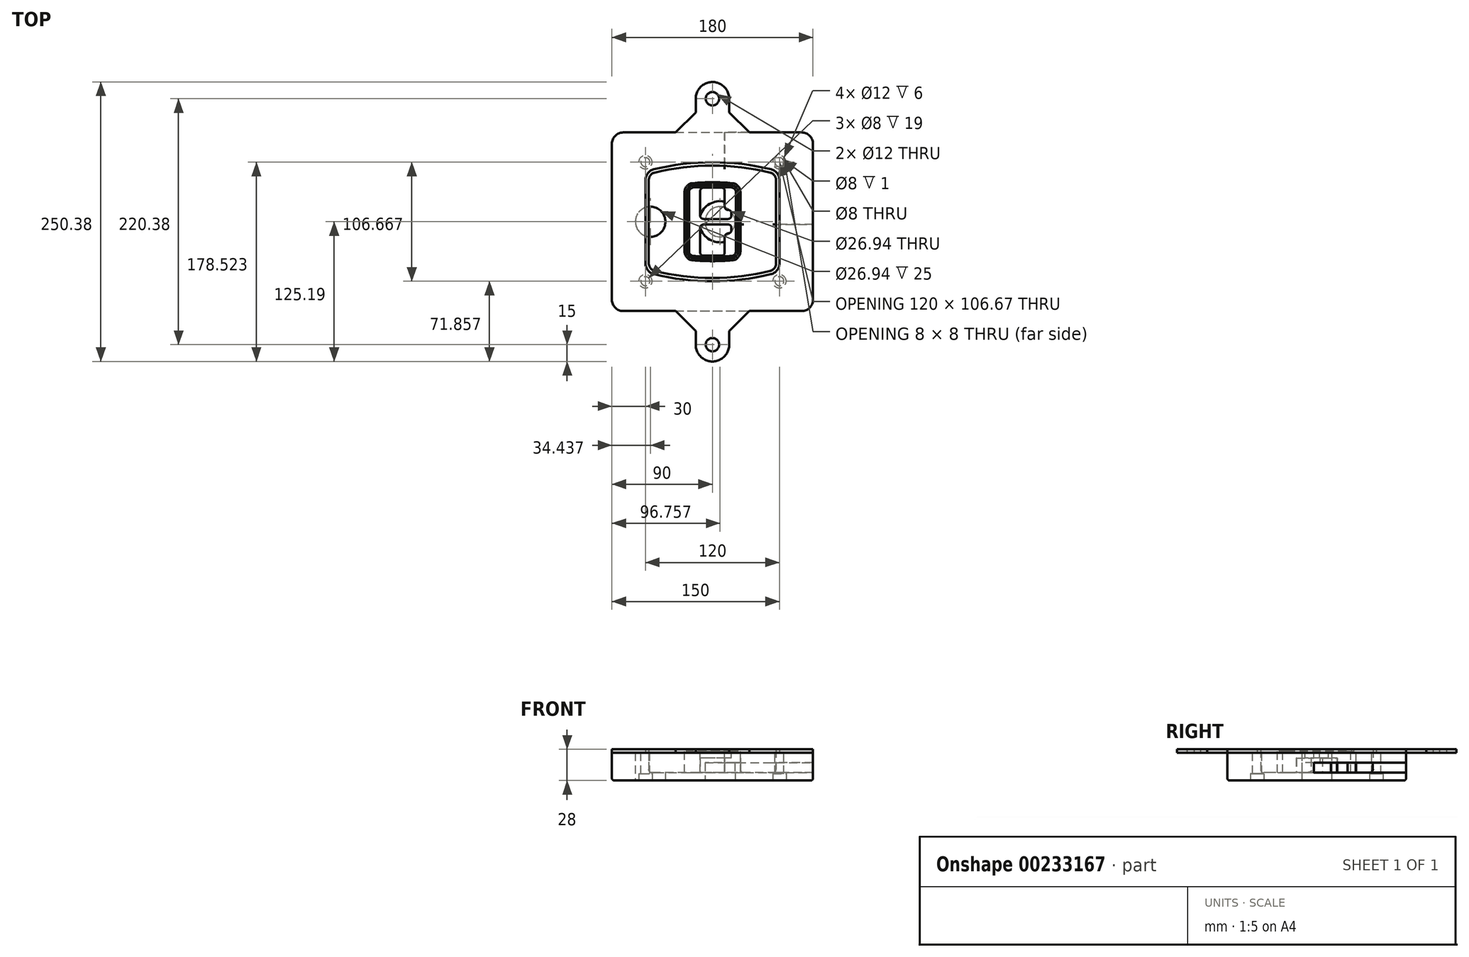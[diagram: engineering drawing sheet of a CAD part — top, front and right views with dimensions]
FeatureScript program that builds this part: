
annotation { "Feature Type Name" : "Feature", "Feature Type Description" : "" }
export const myFeature = defineFeature(function(context is Context, id is Id, definition is map)
    precondition{}
    {
        {
            var Q0;
            Q0=qCreatedBy(makeId("Top.planeOp"),FACE);
            var sketch = newSketch(context, id + "F0", { "sketchPlane" : qUnion([Q0])});
            skPoint(sketch, "E0.rect.middle", {"position": v(0, 0) * mm});
            skLineSegment(sketch, "E1.bottom", {"start": v(-80, -80) * mm, "end": v(80, -80) * mm});
            skLineSegment(sketch, "E1.top", {"start": v(-80, 80) * mm, "end": v(80, 80) * mm});
            skLineSegment(sketch, "E1.left", {"start": v(-90, -70) * mm, "end": v(-90, 70) * mm});
            skLineSegment(sketch, "E1.right", {"start": v(90, -70) * mm, "end": v(90, 70) * mm});
            skLineSegment(sketch, "E2", {"start": v(-90, 80) * mm, "end": v(90, -80) * mm, "construction": true});
            skLineSegment(sketch, "E3", {"start": v(90, 80) * mm, "end": v(-90, -80) * mm, "construction": true});
            skCircle(sketch, "E4", {"center": v(-60, 53.33) * mm, "radius": 4 * mm});
            skCircle(sketch, "E5", {"center": v(60, 53.33) * mm, "radius": 4 * mm});
            skCircle(sketch, "E6", {"center": v(60, -53.33) * mm, "radius": 4 * mm});
            skCircle(sketch, "E7", {"center": v(-60, -53.33) * mm, "radius": 4 * mm});
            skLineSegment(sketch, "E8", {"start": v(-60, 53.33) * mm, "end": v(60, 53.33) * mm, "construction": true});
            skLineSegment(sketch, "E9", {"start": v(60, 53.33) * mm, "end": v(60, -53.33) * mm, "construction": true});
            skLineSegment(sketch, "E10", {"start": v(60, -53.33) * mm, "end": v(-60, -53.33) * mm, "construction": true});
            skLineSegment(sketch, "E11", {"start": v(-60, -53.33) * mm, "end": v(-60, 53.33) * mm, "construction": true});
            skLineSegment(sketch, "E12", {"start": v(-60, 37.3) * mm, "end": v(-60, -37.3) * mm});
            skLineSegment(sketch, "E13", {"start": v(60, 37.3) * mm, "end": v(60, -37.3) * mm});
            skArc(sketch, "E14", {"start": v(52.38, 47.01) * mm, "mid": v(0, 53.33) * mm, "end": v(-52.38, 47.01) * mm});
            skArc(sketch, "E15", {"start": v(-52.38, -47.01) * mm, "mid": v(0, -53.33) * mm, "end": v(52.38, -47.01) * mm});
            skLineSegment(sketch, "E16", {"start": v(-60, 0) * mm, "end": v(60, 0) * mm, "construction": true});
            skPoint(sketch, "E17.visualSharp", {"position": v(-60, -45) * mm});
            skArc(sketch, "E17.filletArc", {"start": v(-60, -37.3) * mm, "mid": v(-57.87, -43.47) * mm, "end": v(-52.38, -47.01) * mm});
            skPoint(sketch, "E18.visualSharp", {"position": v(-60, 45) * mm});
            skArc(sketch, "E18.filletArc", {"start": v(-52.38, 47.01) * mm, "mid": v(-57.87, 43.47) * mm, "end": v(-60, 37.3) * mm});
            skPoint(sketch, "E19.visualSharp", {"position": v(60, 45) * mm});
            skArc(sketch, "E19.filletArc", {"start": v(60, 37.3) * mm, "mid": v(57.87, 43.47) * mm, "end": v(52.38, 47.01) * mm});
            skPoint(sketch, "E20.visualSharp", {"position": v(60, -45) * mm});
            skArc(sketch, "E20.filletArc", {"start": v(52.38, -47.01) * mm, "mid": v(57.87, -43.47) * mm, "end": v(60, -37.3) * mm});
            skPoint(sketch, "E21.visualSharp", {"position": v(-90, 80) * mm});
            skArc(sketch, "E21.filletArc", {"start": v(-80, 80) * mm, "mid": v(-87.07, 77.07) * mm, "end": v(-90, 70) * mm});
            skPoint(sketch, "E22.visualSharp", {"position": v(90, 80) * mm});
            skArc(sketch, "E22.filletArc", {"start": v(90, 70) * mm, "mid": v(87.07, 77.07) * mm, "end": v(80, 80) * mm});
            skPoint(sketch, "E23.visualSharp", {"position": v(90, -80) * mm});
            skArc(sketch, "E23.filletArc", {"start": v(80, -80) * mm, "mid": v(87.07, -77.07) * mm, "end": v(90, -70) * mm});
            skPoint(sketch, "E24.visualSharp", {"position": v(-90, -80) * mm});
            skArc(sketch, "E24.filletArc", {"start": v(-90, -70) * mm, "mid": v(-87.07, -77.07) * mm, "end": v(-80, -80) * mm});
            skArc(sketch, "E25.0", {"start": v(57, 37.3) * mm, "mid": v(55.5, 41.62) * mm, "end": v(51.67, 44.1) * mm});
            skLineSegment(sketch, "E25.1", {"start": v(57, 37.3) * mm, "end": v(57, -37.3) * mm});
            skArc(sketch, "E25.2", {"start": v(51.67, -44.1) * mm, "mid": v(55.5, -41.62) * mm, "end": v(57, -37.3) * mm});
            skArc(sketch, "E25.3", {"start": v(-51.67, -44.1) * mm, "mid": v(0, -50.33) * mm, "end": v(51.67, -44.1) * mm});
            skArc(sketch, "E25.4", {"start": v(-57, -37.3) * mm, "mid": v(-55.5, -41.62) * mm, "end": v(-51.67, -44.1) * mm});
            skArc(sketch, "E25.5", {"start": v(51.67, 44.1) * mm, "mid": v(0, 50.33) * mm, "end": v(-51.67, 44.1) * mm});
            skLineSegment(sketch, "E25.6", {"start": v(-57, 37.3) * mm, "end": v(-57, -37.3) * mm});
            skArc(sketch, "E25.7", {"start": v(-51.67, 44.1) * mm, "mid": v(-55.5, 41.62) * mm, "end": v(-57, 37.3) * mm});
            skArc(sketch, "E26.0", {"start": v(-53.33, 50.9) * mm, "mid": v(-61.01, 45.94) * mm, "end": v(-64, 37.3) * mm});
            skArc(sketch, "E26.1", {"start": v(53.33, 50.9) * mm, "mid": v(0, 57.33) * mm, "end": v(-53.33, 50.9) * mm});
            skArc(sketch, "E26.2", {"start": v(64, 37.3) * mm, "mid": v(61.01, 45.94) * mm, "end": v(53.33, 50.9) * mm});
            skLineSegment(sketch, "E26.3", {"start": v(64, 37.3) * mm, "end": v(64, -37.3) * mm});
            skArc(sketch, "E26.4", {"start": v(53.33, -50.9) * mm, "mid": v(61.01, -45.94) * mm, "end": v(64, -37.3) * mm});
            skLineSegment(sketch, "E26.5", {"start": v(-64, 37.3) * mm, "end": v(-64, -37.3) * mm});
            skArc(sketch, "E26.6", {"start": v(-53.33, -50.9) * mm, "mid": v(0, -57.33) * mm, "end": v(53.33, -50.9) * mm});
            skArc(sketch, "E26.7", {"start": v(-64, -37.3) * mm, "mid": v(-61.01, -45.94) * mm, "end": v(-53.33, -50.9) * mm});
            skSolve(sketch);
        }
        {
            var Q0;
            Q0=makeQuery(id+"F0.imprint","IMPRINT",FACE,{"disambiguationData":[TD([[makeQuery(id+"F0.imprint","IMPRINT",EDGE,{"derivedFrom":sQuery(id+"F0.wireOp",EDGE,"E1.bottom")}),1.0]])]});
            var Q1;
            Q1=makeQuery(id+"F0.imprint","IMPRINT",FACE,{"disambiguationData":[TD([[makeQuery(id+"F0.imprint","IMPRINT",EDGE,{"derivedFrom":sQuery(id+"F0.wireOp",EDGE,"E12")}),1.0]])]});
            var Q2;
            Q2=makeQuery(id+"F0.imprint","IMPRINT",FACE,{"disambiguationData":[TD([[makeQuery(id+"F0.imprint","IMPRINT",EDGE,{"derivedFrom":sQuery(id+"F0.wireOp",EDGE,"E25.0")}),1.0]])]});
            var Q3;
            Q3=makeQuery(id+"F0.imprint","IMPRINT",FACE,{"disambiguationData":[TD([[makeQuery(id+"F0.imprint","IMPRINT",EDGE,{"derivedFrom":sQuery(id+"F0.wireOp",EDGE,"E12")}),-1.0]])]});
            extrude(context, id + "F1", {"entities" : qUnion([Q0, Q1, Q2, Q3]), "oppositeDirection" : true, "depth" : 25 * mm});
        }
        {
            var Q0;
            Q0=makeQuery(id+"F0.imprint","IMPRINT",FACE,{"disambiguationData":[TD([[makeQuery(id+"F0.imprint","IMPRINT",EDGE,{"derivedFrom":sQuery(id+"F0.wireOp",EDGE,"E12")}),1.0]])]});
            extrude(context, id + "F2", {"entities" : qUnion([Q0]), "operationType" : NewBodyOperationType.ADD, "depth" : 3 * mm});
        }
        {
            var Q0;
            Q0=makeQuery(id+"F0.imprint","IMPRINT",FACE,{"disambiguationData":[TD([[makeQuery(id+"F0.imprint","IMPRINT",EDGE,{"derivedFrom":sQuery(id+"F0.wireOp",EDGE,"E25.0")}),1.0]])]});
            extrude(context, id + "F3", {"entities" : qUnion([Q0]), "operationType" : NewBodyOperationType.REMOVE, "oppositeDirection" : true, "depth" : 18 * mm});
        }
        {
            var Q0;
            Q0=makeQuery(id+"F2.opExtrude","CAP_FACE",FACE,{"disambiguationData":[OSD([sQuery(id+"F0.wireOp",EDGE,"E12"),sQuery(id+"F0.wireOp",EDGE,"E13"),sQuery(id+"F0.wireOp",EDGE,"E14"),sQuery(id+"F0.wireOp",EDGE,"E15"),sQuery(id+"F0.wireOp",EDGE,"E17.filletArc"),sQuery(id+"F0.wireOp",EDGE,"E18.filletArc"),sQuery(id+"F0.wireOp",EDGE,"E19.filletArc"),sQuery(id+"F0.wireOp",EDGE,"E20.filletArc"),sQuery(id+"F0.wireOp",EDGE,"E25.0"),sQuery(id+"F0.wireOp",EDGE,"E25.1"),sQuery(id+"F0.wireOp",EDGE,"E25.2"),sQuery(id+"F0.wireOp",EDGE,"E25.3"),sQuery(id+"F0.wireOp",EDGE,"E25.4"),sQuery(id+"F0.wireOp",EDGE,"E25.5"),sQuery(id+"F0.wireOp",EDGE,"E25.6"),sQuery(id+"F0.wireOp",EDGE,"E25.7")])],"isStart":false});
            var sketch = newSketch(context, id + "F4", { "sketchPlane" : qUnion([Q0])});
            skArc(sketch, "E27.0", {"start": v(-17.7, -34.56) * mm, "mid": v(0, -35.33) * mm, "end": v(17.7, -34.56) * mm});
            skArc(sketch, "E28.0", {"start": v(17.7, 34.56) * mm, "mid": v(0, 35.33) * mm, "end": v(-17.7, 34.56) * mm});
            skLineSegment(sketch, "E29", {"start": v(-25, 26.59) * mm, "end": v(-25, -26.59) * mm});
            skLineSegment(sketch, "E30", {"start": v(25, 26.59) * mm, "end": v(25, -26.59) * mm});
            skLineSegment(sketch, "E31", {"start": v(-25, 33.78) * mm, "end": v(25, 33.78) * mm, "construction": true});
            skLineSegment(sketch, "E32", {"start": v(-25, -33.78) * mm, "end": v(25, -33.78) * mm, "construction": true});
            skPoint(sketch, "E33.visualSharp", {"position": v(-25, 33.78) * mm});
            skArc(sketch, "E33.filletArc", {"start": v(-17.7, 34.56) * mm, "mid": v(-22.9, 32) * mm, "end": v(-25, 26.59) * mm});
            skPoint(sketch, "E34.visualSharp", {"position": v(25, 33.78) * mm});
            skArc(sketch, "E34.filletArc", {"start": v(25, 26.59) * mm, "mid": v(22.9, 32) * mm, "end": v(17.7, 34.56) * mm});
            skPoint(sketch, "E35.visualSharp", {"position": v(25, -33.78) * mm});
            skArc(sketch, "E35.filletArc", {"start": v(17.7, -34.56) * mm, "mid": v(22.9, -32) * mm, "end": v(25, -26.59) * mm});
            skPoint(sketch, "E36.visualSharp", {"position": v(-25, -33.78) * mm});
            skArc(sketch, "E36.filletArc", {"start": v(-25, -26.59) * mm, "mid": v(-22.9, -32) * mm, "end": v(-17.7, -34.56) * mm});
            skArc(sketch, "E37.0", {"start": v(51.67, 44.1) * mm, "mid": v(0, 50.33) * mm, "end": v(-51.67, 44.1) * mm});
            skArc(sketch, "E37.1", {"start": v(-51.67, 44.1) * mm, "mid": v(-55.5, 41.62) * mm, "end": v(-57, 37.3) * mm});
            skLineSegment(sketch, "E37.2", {"start": v(-57, 37.3) * mm, "end": v(-57, -37.3) * mm});
            skArc(sketch, "E37.3", {"start": v(-57, -37.3) * mm, "mid": v(-55.5, -41.62) * mm, "end": v(-51.67, -44.1) * mm});
            skArc(sketch, "E37.4", {"start": v(-51.67, -44.1) * mm, "mid": v(0, -50.33) * mm, "end": v(51.67, -44.1) * mm});
            skArc(sketch, "E37.5", {"start": v(51.67, -44.1) * mm, "mid": v(55.5, -41.62) * mm, "end": v(57, -37.3) * mm});
            skLineSegment(sketch, "E37.6", {"start": v(57, 37.3) * mm, "end": v(57, -37.3) * mm});
            skArc(sketch, "E37.7", {"start": v(57, 37.3) * mm, "mid": v(55.5, 41.62) * mm, "end": v(51.67, 44.1) * mm});
            skLineSegment(sketch, "E38.0", {"start": v(23, 26.59) * mm, "end": v(23, -26.59) * mm});
            skArc(sketch, "E38.1", {"start": v(17.53, -32.56) * mm, "mid": v(21.42, -30.64) * mm, "end": v(23, -26.59) * mm});
            skArc(sketch, "E38.2", {"start": v(-17.53, -32.56) * mm, "mid": v(0, -33.33) * mm, "end": v(17.53, -32.56) * mm});
            skArc(sketch, "E38.3", {"start": v(-23, -26.59) * mm, "mid": v(-21.42, -30.64) * mm, "end": v(-17.53, -32.56) * mm});
            skLineSegment(sketch, "E38.4", {"start": v(-23, 26.59) * mm, "end": v(-23, -26.59) * mm});
            skArc(sketch, "E38.5", {"start": v(23, 26.59) * mm, "mid": v(21.42, 30.64) * mm, "end": v(17.53, 32.56) * mm});
            skArc(sketch, "E38.6", {"start": v(-17.53, 32.56) * mm, "mid": v(-21.42, 30.64) * mm, "end": v(-23, 26.59) * mm});
            skArc(sketch, "E38.7", {"start": v(17.53, 32.56) * mm, "mid": v(0, 33.33) * mm, "end": v(-17.53, 32.56) * mm});
            skArc(sketch, "E39.0", {"start": v(21, 26.59) * mm, "mid": v(19.95, 29.29) * mm, "end": v(17.35, 30.57) * mm});
            skLineSegment(sketch, "E39.1", {"start": v(21, 26.59) * mm, "end": v(21, -26.59) * mm});
            skArc(sketch, "E39.2", {"start": v(17.35, -30.57) * mm, "mid": v(19.95, -29.29) * mm, "end": v(21, -26.59) * mm});
            skArc(sketch, "E39.3", {"start": v(-17.35, -30.57) * mm, "mid": v(0, -31.33) * mm, "end": v(17.35, -30.57) * mm});
            skArc(sketch, "E39.4", {"start": v(-21, -26.59) * mm, "mid": v(-19.95, -29.29) * mm, "end": v(-17.35, -30.57) * mm});
            skArc(sketch, "E39.5", {"start": v(17.35, 30.57) * mm, "mid": v(0, 31.33) * mm, "end": v(-17.35, 30.57) * mm});
            skLineSegment(sketch, "E39.6", {"start": v(-21, 26.59) * mm, "end": v(-21, -26.59) * mm});
            skArc(sketch, "E39.7", {"start": v(-17.35, 30.57) * mm, "mid": v(-19.95, 29.29) * mm, "end": v(-21, 26.59) * mm});
            skLineSegment(sketch, "E40", {"start": v(-25, 0) * mm, "end": v(25, 0) * mm, "construction": true});
            skLineSegment(sketch, "E41", {"start": v(-11, 5.5) * mm, "end": v(-11, 27.5) * mm});
            skLineSegment(sketch, "E42", {"start": v(-8, 30.5) * mm, "end": v(8, 30.5) * mm});
            skLineSegment(sketch, "E43", {"start": v(11, 27.5) * mm, "end": v(11, 13.5) * mm});
            skLineSegment(sketch, "E44", {"start": v(14, 10.5) * mm, "end": v(14, 10.5) * mm});
            skLineSegment(sketch, "E45", {"start": v(17, 7.5) * mm, "end": v(17, 5.5) * mm});
            skLineSegment(sketch, "E46", {"start": v(14, 2.5) * mm, "end": v(-8, 2.5) * mm});
            skPoint(sketch, "E47.visualSharp", {"position": v(-11, 30.5) * mm});
            skArc(sketch, "E47.filletArc", {"start": v(-8, 30.5) * mm, "mid": v(-10.12, 29.62) * mm, "end": v(-11, 27.5) * mm});
            skPoint(sketch, "E48.visualSharp", {"position": v(11, 30.5) * mm});
            skArc(sketch, "E48.filletArc", {"start": v(11, 27.5) * mm, "mid": v(10.12, 29.62) * mm, "end": v(8, 30.5) * mm});
            skPoint(sketch, "E49.visualSharp", {"position": v(11, 10.5) * mm});
            skArc(sketch, "E49.filletArc", {"start": v(11, 13.5) * mm, "mid": v(11.88, 11.38) * mm, "end": v(14, 10.5) * mm});
            skPoint(sketch, "E50.visualSharp", {"position": v(17, 10.5) * mm});
            skArc(sketch, "E50.filletArc", {"start": v(17, 7.5) * mm, "mid": v(16.12, 9.62) * mm, "end": v(14, 10.5) * mm});
            skPoint(sketch, "E51.visualSharp", {"position": v(17, 2.5) * mm});
            skArc(sketch, "E51.filletArc", {"start": v(14, 2.5) * mm, "mid": v(16.12, 3.38) * mm, "end": v(17, 5.5) * mm});
            skPoint(sketch, "E52.visualSharp", {"position": v(-11, 2.5) * mm});
            skArc(sketch, "E52.filletArc", {"start": v(-11, 5.5) * mm, "mid": v(-10.12, 3.38) * mm, "end": v(-8, 2.5) * mm});
            skLineSegment(sketch, "E53.0.MirrorCS", {"start": v(14, -2.5) * mm, "end": v(-8, -2.5) * mm});
            skArc(sketch, "E54.0.MirrorCS", {"start": v(-11, -5.5) * mm, "mid": v(-10.12, -3.38) * mm, "end": v(-8, -2.5) * mm});
            skLineSegment(sketch, "E55.0.MirrorCS", {"start": v(-11, -5.5) * mm, "end": v(-11, -27.5) * mm});
            skArc(sketch, "E56.0.MirrorCS", {"start": v(-8, -30.5) * mm, "mid": v(-10.12, -29.62) * mm, "end": v(-11, -27.5) * mm});
            skLineSegment(sketch, "E57.0.MirrorCS", {"start": v(-8, -30.5) * mm, "end": v(8, -30.5) * mm});
            skArc(sketch, "E58.0.MirrorCS", {"start": v(11, -27.5) * mm, "mid": v(10.12, -29.62) * mm, "end": v(8, -30.5) * mm});
            skLineSegment(sketch, "E59.0.MirrorCS", {"start": v(11, -27.5) * mm, "end": v(11, -13.5) * mm});
            skArc(sketch, "E60.0.MirrorCS", {"start": v(11, -13.5) * mm, "mid": v(11.88, -11.38) * mm, "end": v(14, -10.5) * mm});
            skArc(sketch, "E61.0.MirrorCS", {"start": v(17, -7.5) * mm, "mid": v(16.12, -9.62) * mm, "end": v(14, -10.5) * mm});
            skLineSegment(sketch, "E62.0.MirrorCS", {"start": v(17, -7.5) * mm, "end": v(17, -5.5) * mm});
            skArc(sketch, "E63.0.MirrorCS", {"start": v(14, -2.5) * mm, "mid": v(16.12, -3.38) * mm, "end": v(17, -5.5) * mm});
            skSolve(sketch);
        }
        {
            var Q0;
            Q0=makeQuery(id+"F4.imprint","IMPRINT",FACE,{"disambiguationData":[TD([[makeQuery(id+"F4.imprint","IMPRINT",EDGE,{"derivedFrom":sQuery(id+"F4.wireOp",EDGE,"E27.0")}),1.0]])]});
            var Q1;
            Q1=makeQuery(id+"F4.imprint","IMPRINT",FACE,{"disambiguationData":[TD([[makeQuery(id+"F4.imprint","IMPRINT",EDGE,{"derivedFrom":sQuery(id+"F4.wireOp",EDGE,"E38.0")}),-1.0]])]});
            var Q2;
            Q2=makeQuery(id+"F4.imprint","IMPRINT",FACE,{"disambiguationData":[TD([[makeQuery(id+"F4.imprint","IMPRINT",EDGE,{"derivedFrom":sQuery(id+"F4.wireOp",EDGE,"E39.0")}),1.0]])]});
            extrude(context, id + "F5", {"entities" : qUnion([Q0, Q1, Q2]), "operationType" : NewBodyOperationType.ADD, "endBound" : BoundingType.UP_TO_NEXT, "oppositeDirection" : true, "depth" : 25 * mm});
        }
        {
            var Q0;
            Q0=makeQuery(id+"F4.imprint","IMPRINT",FACE,{"disambiguationData":[TD([[makeQuery(id+"F4.imprint","IMPRINT",EDGE,{"derivedFrom":sQuery(id+"F4.wireOp",EDGE,"E38.0")}),-1.0]])]});
            extrude(context, id + "F6", {"entities" : qUnion([Q0]), "operationType" : NewBodyOperationType.REMOVE, "oppositeDirection" : true, "depth" : 2 * mm});
        }
        {
            var Q0;
            Q0=makeQuery(id+"F1.opExtrude","CAP_FACE",FACE,{"disambiguationData":[OSD([sQuery(id+"F0.wireOp",EDGE,"E1.bottom"),sQuery(id+"F0.wireOp",EDGE,"E1.top"),sQuery(id+"F0.wireOp",EDGE,"E1.left"),sQuery(id+"F0.wireOp",EDGE,"E1.right"),sQuery(id+"F0.wireOp",EDGE,"E4"),sQuery(id+"F0.wireOp",EDGE,"E5"),sQuery(id+"F0.wireOp",EDGE,"E6"),sQuery(id+"F0.wireOp",EDGE,"E7"),sQuery(id+"F0.wireOp",EDGE,"E21.filletArc"),sQuery(id+"F0.wireOp",EDGE,"E22.filletArc"),sQuery(id+"F0.wireOp",EDGE,"E23.filletArc"),sQuery(id+"F0.wireOp",EDGE,"E24.filletArc")])],"isStart":false});
            var sketch = newSketch(context, id + "F7", { "sketchPlane" : qUnion([Q0])});
            skCircle(sketch, "E64", {"center": v(6.76, 0) * mm, "radius": 13.47 * mm});
            skCircle(sketch, "E65", {"center": v(-55.56, 0) * mm, "radius": 13.47 * mm});
            skLineSegment(sketch, "E66", {"start": v(90, 0) * mm, "end": v(-90, 0) * mm});
            skCircle(sketch, "E67", {"center": v(6.76, 0) * mm, "radius": 18.47 * mm});
            skCircle(sketch, "E68", {"center": v(60, -53.33) * mm, "radius": 6 * mm});
            skCircle(sketch, "E69", {"center": v(-60, -53.33) * mm, "radius": 6 * mm});
            skCircle(sketch, "E70", {"center": v(-60, 53.33) * mm, "radius": 6 * mm});
            skCircle(sketch, "E71", {"center": v(60, 53.33) * mm, "radius": 6 * mm});
            skSolve(sketch);
        }
        {
            var Q0;
            {var subQ1=sQuery(id+"F7.wireOp",EDGE,"E66");var subQ4=sQuery(id+"F7.wireOp",EDGE,"E64");var subQ6=makeQuery(id+"F7.imprint","INTERSECT",VERTEX,{"disambiguationData":[OD(0.0)],"derivedFrom":[subQ4,subQ1]});Q0=makeQuery(id+"F7.imprint","IMPRINT",FACE,{"disambiguationData":[TD([[makeQuery(id+"F7.imprint","IMPRINT",EDGE,{"disambiguationData":[TD([[subQ6,-1.0]])],"derivedFrom":subQ4}),-1.0]])]});}
            var Q1;
            {var subQ0=sQuery(id+"F7.wireOp",EDGE,"E66");var subQ1=sQuery(id+"F7.wireOp",EDGE,"E64");var subQ3=makeQuery(id+"F7.imprint","INTERSECT",VERTEX,{"disambiguationData":[OD(0.0)],"derivedFrom":[subQ1,subQ0]});Q1=makeQuery(id+"F7.imprint","IMPRINT",FACE,{"disambiguationData":[TD([[makeQuery(id+"F7.imprint","IMPRINT",EDGE,{"disambiguationData":[TD([[subQ3,-1.0]])],"derivedFrom":subQ1}),1.0]])]});}
            var Q2;
            {var subQ0=sQuery(id+"F7.wireOp",EDGE,"E66");var subQ1=sQuery(id+"F7.wireOp",EDGE,"E64");var subQ3=makeQuery(id+"F7.imprint","INTERSECT",VERTEX,{"disambiguationData":[OD(0.0)],"derivedFrom":[subQ1,subQ0]});Q2=makeQuery(id+"F7.imprint","IMPRINT",FACE,{"disambiguationData":[TD([[makeQuery(id+"F7.imprint","IMPRINT",EDGE,{"disambiguationData":[TD([[subQ3,1.0]])],"derivedFrom":subQ1}),1.0]])]});}
            var Q3;
            {var subQ1=sQuery(id+"F7.wireOp",EDGE,"E66");var subQ4=sQuery(id+"F7.wireOp",EDGE,"E64");var subQ6=makeQuery(id+"F7.imprint","INTERSECT",VERTEX,{"disambiguationData":[OD(0.0)],"derivedFrom":[subQ4,subQ1]});Q3=makeQuery(id+"F7.imprint","IMPRINT",FACE,{"disambiguationData":[TD([[makeQuery(id+"F7.imprint","IMPRINT",EDGE,{"disambiguationData":[TD([[subQ6,1.0]])],"derivedFrom":subQ4}),-1.0]])]});}
            extrude(context, id + "F8", {"entities" : qUnion([Q0, Q1, Q2, Q3]), "operationType" : NewBodyOperationType.ADD, "oppositeDirection" : true, "depth" : 20 * mm});
        }
        {
            var Q0;
            {var subQ0=sQuery(id+"F7.wireOp",EDGE,"E66");var subQ1=sQuery(id+"F7.wireOp",EDGE,"E64");var subQ3=makeQuery(id+"F7.imprint","INTERSECT",VERTEX,{"disambiguationData":[OD(0.0)],"derivedFrom":[subQ1,subQ0]});Q0=makeQuery(id+"F7.imprint","IMPRINT",FACE,{"disambiguationData":[TD([[makeQuery(id+"F7.imprint","IMPRINT",EDGE,{"disambiguationData":[TD([[subQ3,-1.0]])],"derivedFrom":subQ1}),1.0]])]});}
            var Q1;
            {var subQ0=sQuery(id+"F7.wireOp",EDGE,"E66");var subQ1=sQuery(id+"F7.wireOp",EDGE,"E64");var subQ3=makeQuery(id+"F7.imprint","INTERSECT",VERTEX,{"disambiguationData":[OD(0.0)],"derivedFrom":[subQ1,subQ0]});Q1=makeQuery(id+"F7.imprint","IMPRINT",FACE,{"disambiguationData":[TD([[makeQuery(id+"F7.imprint","IMPRINT",EDGE,{"disambiguationData":[TD([[subQ3,1.0]])],"derivedFrom":subQ1}),1.0]])]});}
            extrude(context, id + "F9", {"entities" : qUnion([Q0, Q1]), "operationType" : NewBodyOperationType.REMOVE, "oppositeDirection" : true, "depth" : 16 * mm});
        }
        {
            var Q0;
            {var subQ0=sQuery(id+"F7.wireOp",EDGE,"E66");var subQ1=sQuery(id+"F7.wireOp",EDGE,"E65");var subQ3=makeQuery(id+"F7.imprint","INTERSECT",VERTEX,{"disambiguationData":[OD(0.0)],"derivedFrom":[subQ1,subQ0]});Q0=makeQuery(id+"F7.imprint","IMPRINT",FACE,{"disambiguationData":[TD([[makeQuery(id+"F7.imprint","IMPRINT",EDGE,{"disambiguationData":[TD([[subQ3,-1.0]])],"derivedFrom":subQ1}),1.0]])]});}
            var Q1;
            {var subQ0=sQuery(id+"F7.wireOp",EDGE,"E66");var subQ1=sQuery(id+"F7.wireOp",EDGE,"E65");var subQ3=makeQuery(id+"F7.imprint","INTERSECT",VERTEX,{"disambiguationData":[OD(0.0)],"derivedFrom":[subQ1,subQ0]});Q1=makeQuery(id+"F7.imprint","IMPRINT",FACE,{"disambiguationData":[TD([[makeQuery(id+"F7.imprint","IMPRINT",EDGE,{"disambiguationData":[TD([[subQ3,1.0]])],"derivedFrom":subQ1}),1.0]])]});}
            extrude(context, id + "F10", {"entities" : qUnion([Q0, Q1]), "operationType" : NewBodyOperationType.REMOVE, "oppositeDirection" : true, "depth" : 25 * mm});
        }
        {
            var Q0;
            Q0=makeQuery(id+"F7.imprint","IMPRINT",FACE,{"disambiguationData":[TD([[makeQuery(id+"F7.imprint","IMPRINT",EDGE,{"derivedFrom":sQuery(id+"F7.wireOp",EDGE,"E68")}),1.0]])]});
            var Q1;
            Q1=makeQuery(id+"F7.imprint","IMPRINT",FACE,{"disambiguationData":[TD([[makeQuery(id+"F7.imprint","IMPRINT",EDGE,{"derivedFrom":makeQuery(id+"F1.opExtrude","CAP_EDGE",EDGE,{"disambiguationData":[OSD([sQuery(id+"F0.wireOp",EDGE,"E5")])],"isStart":false})}),-1.0]])]});
            var Q2;
            Q2=makeQuery(id+"F7.imprint","IMPRINT",FACE,{"disambiguationData":[TD([[makeQuery(id+"F7.imprint","IMPRINT",EDGE,{"derivedFrom":sQuery(id+"F7.wireOp",EDGE,"E69")}),1.0]])]});
            var Q3;
            Q3=makeQuery(id+"F7.imprint","IMPRINT",FACE,{"disambiguationData":[TD([[makeQuery(id+"F7.imprint","IMPRINT",EDGE,{"derivedFrom":makeQuery(id+"F1.opExtrude","CAP_EDGE",EDGE,{"disambiguationData":[OSD([sQuery(id+"F0.wireOp",EDGE,"E4")])],"isStart":false})}),-1.0]])]});
            var Q4;
            Q4=makeQuery(id+"F7.imprint","IMPRINT",FACE,{"disambiguationData":[TD([[makeQuery(id+"F7.imprint","IMPRINT",EDGE,{"derivedFrom":sQuery(id+"F7.wireOp",EDGE,"E70")}),1.0]])]});
            var Q5;
            Q5=makeQuery(id+"F7.imprint","IMPRINT",FACE,{"disambiguationData":[TD([[makeQuery(id+"F7.imprint","IMPRINT",EDGE,{"derivedFrom":makeQuery(id+"F1.opExtrude","CAP_EDGE",EDGE,{"disambiguationData":[OSD([sQuery(id+"F0.wireOp",EDGE,"E7")])],"isStart":false})}),-1.0]])]});
            var Q6;
            Q6=makeQuery(id+"F7.imprint","IMPRINT",FACE,{"disambiguationData":[TD([[makeQuery(id+"F7.imprint","IMPRINT",EDGE,{"derivedFrom":sQuery(id+"F7.wireOp",EDGE,"E71")}),1.0]])]});
            var Q7;
            Q7=makeQuery(id+"F7.imprint","IMPRINT",FACE,{"disambiguationData":[TD([[makeQuery(id+"F7.imprint","IMPRINT",EDGE,{"derivedFrom":makeQuery(id+"F1.opExtrude","CAP_EDGE",EDGE,{"disambiguationData":[OSD([sQuery(id+"F0.wireOp",EDGE,"E6")])],"isStart":false})}),-1.0]])]});
            extrude(context, id + "F11", {"entities" : qUnion([Q0, Q1, Q2, Q3, Q4, Q5, Q6, Q7]), "operationType" : NewBodyOperationType.REMOVE, "oppositeDirection" : true, "depth" : 6 * mm});
        }
        {
            var Q0;
            Q0=makeQuery(id+"F9.boolean.opBoolean","COPY",FACE,{"derivedFrom":makeQuery(id+"F9.opExtrude","CAP_FACE",FACE,{"disambiguationData":[OSD([sQuery(id+"F7.wireOp",EDGE,"E64")])],"isStart":false})});
            var sketch = newSketch(context, id + "F12", { "sketchPlane" : qUnion([Q0])});
            skArc(sketch, "E72.0", {"start": v(11, -88.19) * mm, "mid": v(97.1, -83.6) * mm, "end": v(92.5, 2.5) * mm});
            skLineSegment(sketch, "E72.1", {"start": v(11, -17.97) * mm, "end": v(11, -17.97) * mm});
            skLineSegment(sketch, "E73", {"start": v(92.5, -105.13) * mm, "end": v(102.3, -105.13) * mm});
            skLineSegment(sketch, "E74.0", {"start": v(92.5, 2.5) * mm, "end": v(14, 2.5) * mm});
            skArc(sketch, "E74.1", {"start": v(14, 2.5) * mm, "mid": v(16.12, 3.38) * mm, "end": v(17, 5.5) * mm});
            skLineSegment(sketch, "E74.2", {"start": v(17, 7.5) * mm, "end": v(17, 5.5) * mm});
            skArc(sketch, "E74.3", {"start": v(17, 7.5) * mm, "mid": v(16.12, 9.62) * mm, "end": v(14, 10.5) * mm});
            skArc(sketch, "E74.4", {"start": v(11, 13.5) * mm, "mid": v(11.88, 11.38) * mm, "end": v(14, 10.5) * mm});
            skLineSegment(sketch, "E74.5", {"start": v(11, 13.5) * mm, "end": v(11, -88.19) * mm});
            skLineSegment(sketch, "E74.7", {"start": v(92.5, -2.5) * mm, "end": v(14, -2.5) * mm});
            skArc(sketch, "E74.8", {"start": v(14, -2.5) * mm, "mid": v(16.12, -3.38) * mm, "end": v(17, -5.5) * mm});
            skLineSegment(sketch, "E74.9", {"start": v(17, -7.5) * mm, "end": v(17, -5.5) * mm});
            skArc(sketch, "E74.10", {"start": v(17, -7.5) * mm, "mid": v(16.12, -9.62) * mm, "end": v(14, -10.5) * mm});
            skArc(sketch, "E74.11", {"start": v(11, -13.5) * mm, "mid": v(11.88, -11.38) * mm, "end": v(14, -10.5) * mm});
            skLineSegment(sketch, "E74.12", {"start": v(11, -17.97) * mm, "end": v(11, -13.5) * mm});
            skPoint(sketch, "E75.orphan", {"position": v(11, -27.5) * mm});
            skPoint(sketch, "E76.orphan", {"position": v(-8, -2.5) * mm});
            skPoint(sketch, "E77.orphan", {"position": v(-8, 2.5) * mm});
            skPoint(sketch, "E78.orphan", {"position": v(11, 27.5) * mm});
            skSolve(sketch);
        }
        {
            var Q0;
            {var subQ7=sQuery(id+"F12.wireOp",EDGE,"E72.0");var subQ14=sQuery(id+"F12.wireOp",EDGE,"E72.1");var subQ16=sQuery(id+"F12.wireOp",EDGE,"E74.1");var subQ18=sQuery(id+"F12.wireOp",EDGE,"E74.8");Q0=qUnion([makeQuery(id+"F12.imprint","IMPRINT",FACE,{"disambiguationData":[TD([[makeQuery(id+"F12.imprint","IMPRINT",EDGE,{"derivedFrom":subQ7}),1.0]])]}),makeQuery(id+"F12.imprint","IMPRINT",FACE,{"disambiguationData":[TD([[makeQuery(id+"F12.imprint","IMPRINT",EDGE,{"derivedFrom":subQ14}),1.0]])]}),makeQuery(id+"F12.imprint","IMPRINT",FACE,{"disambiguationData":[TD([[makeQuery(id+"F12.imprint","IMPRINT",EDGE,{"derivedFrom":subQ16}),1.0]])]}),makeQuery(id+"F12.imprint","IMPRINT",FACE,{"disambiguationData":[TD([[makeQuery(id+"F12.imprint","IMPRINT",EDGE,{"derivedFrom":subQ18}),-1.0]])]})]);}
            var Q1;
            Q1=makeQuery(id+"F5.boolean.opBoolean","SPLIT",FACE,{"disambiguationData":[TD([makeQuery(id+"F5.opExtrude","SWEPT_FACE",FACE,{"disambiguationData":[OSD([sQuery(id+"F4.wireOp",EDGE,"E41")])]})])],"derivedFrom":makeQuery(id+"F3.boolean.opBoolean","COPY",FACE,{"derivedFrom":makeQuery(id+"F3.opExtrude","CAP_FACE",FACE,{"disambiguationData":[OSD([sQuery(id+"F0.wireOp",EDGE,"E25.0"),sQuery(id+"F0.wireOp",EDGE,"E25.1"),sQuery(id+"F0.wireOp",EDGE,"E25.2"),sQuery(id+"F0.wireOp",EDGE,"E25.3"),sQuery(id+"F0.wireOp",EDGE,"E25.4"),sQuery(id+"F0.wireOp",EDGE,"E25.5"),sQuery(id+"F0.wireOp",EDGE,"E25.6"),sQuery(id+"F0.wireOp",EDGE,"E25.7")])],"isStart":false})})});
            extrude(context, id + "F13", {"entities" : qUnion([Q0]), "operationType" : NewBodyOperationType.REMOVE, "endBound" : BoundingType.UP_TO_SURFACE, "endBoundEntityFace" : qUnion([Q1]), "depth" : 25 * mm});
        }
        {
            var Q0;
            Q0=makeQuery(id+"F3.boolean.opBoolean","COPY",EDGE,{"derivedFrom":makeQuery(id+"F3.opExtrude","CAP_EDGE",EDGE,{"disambiguationData":[OSD([sQuery(id+"F0.wireOp",EDGE,"E25.6")])],"isStart":false})});
            var Q1;
            Q1=makeQuery(id+"F8.boolean.opBoolean","INTERSECT",EDGE,{"derivedFrom":[makeQuery(id+"F5.opExtrude","SWEPT_FACE",FACE,{"disambiguationData":[OSD([sQuery(id+"F4.wireOp",EDGE,"E30")])]}),makeQuery(id+"F8.opExtrude","CAP_FACE",FACE,{"disambiguationData":[OSD([sQuery(id+"F7.wireOp",EDGE,"E67")])],"isStart":false})]});
            var Q2;
            Q2=makeQuery(id+"F8.boolean.opBoolean","INTERSECT",EDGE,{"disambiguationData":[OD(1.0)],"derivedFrom":[makeQuery(id+"F5.opExtrude","SWEPT_FACE",FACE,{"disambiguationData":[OSD([sQuery(id+"F4.wireOp",EDGE,"E30")])]}),makeQuery(id+"F8.opExtrude","SWEPT_FACE",FACE,{"disambiguationData":[OSD([sQuery(id+"F7.wireOp",EDGE,"E67")])]})]});
            var Q3;
            {var subQ0=makeQuery(id+"F3.boolean.opBoolean","COPY",FACE,{"derivedFrom":makeQuery(id+"F3.opExtrude","CAP_FACE",FACE,{"disambiguationData":[OSD([sQuery(id+"F0.wireOp",EDGE,"E25.0"),sQuery(id+"F0.wireOp",EDGE,"E25.1"),sQuery(id+"F0.wireOp",EDGE,"E25.2"),sQuery(id+"F0.wireOp",EDGE,"E25.3"),sQuery(id+"F0.wireOp",EDGE,"E25.4"),sQuery(id+"F0.wireOp",EDGE,"E25.5"),sQuery(id+"F0.wireOp",EDGE,"E25.6"),sQuery(id+"F0.wireOp",EDGE,"E25.7")])],"isStart":false})});var subQ1=sQuery(id+"F4.wireOp",EDGE,"E30");Q3=makeQuery(id+"F8.boolean.opBoolean","SPLIT",EDGE,{"disambiguationData":[TD([makeQuery(id+"F5.opExtrude","SWEPT_FACE",FACE,{"disambiguationData":[OSD([sQuery(id+"F4.wireOp",EDGE,"E35.filletArc")])]})])],"derivedFrom":makeQuery(id+"F5.opExtrude","TWEAK_EDGE",EDGE,{"derivedFrom":[subQ0,makeQuery(id+"F4.imprint","IMPRINT",EDGE,{"derivedFrom":subQ1})]})});}
            var Q4;
            {var subQ0=sQuery(id+"F0.wireOp",EDGE,"E25.0");var subQ1=sQuery(id+"F0.wireOp",EDGE,"E25.1");var subQ2=sQuery(id+"F0.wireOp",EDGE,"E25.2");var subQ3=sQuery(id+"F0.wireOp",EDGE,"E25.3");var subQ4=sQuery(id+"F0.wireOp",EDGE,"E25.4");var subQ5=sQuery(id+"F0.wireOp",EDGE,"E25.5");var subQ6=sQuery(id+"F0.wireOp",EDGE,"E25.6");var subQ7=sQuery(id+"F0.wireOp",EDGE,"E25.7");Q4=makeQuery(id+"F8.boolean.opBoolean","INTERSECT",EDGE,{"derivedFrom":[makeQuery(id+"F5.boolean.opBoolean","SPLIT",FACE,{"disambiguationData":[TD([makeQuery(id+"F2.opExtrude","SWEPT_FACE",FACE,{"disambiguationData":[OSD([subQ0])]})])],"derivedFrom":makeQuery(id+"F3.boolean.opBoolean","COPY",FACE,{"derivedFrom":makeQuery(id+"F3.opExtrude","CAP_FACE",FACE,{"disambiguationData":[OSD([subQ0,subQ1,subQ2,subQ3,subQ4,subQ5,subQ6,subQ7])],"isStart":false})})}),makeQuery(id+"F8.opExtrude","SWEPT_FACE",FACE,{"disambiguationData":[OSD([sQuery(id+"F7.wireOp",EDGE,"E67")])]})]});}
            var Q5;
            Q5=makeQuery(id+"F8.boolean.opBoolean","INTERSECT",EDGE,{"disambiguationData":[OD(0.0)],"derivedFrom":[makeQuery(id+"F5.opExtrude","SWEPT_FACE",FACE,{"disambiguationData":[OSD([sQuery(id+"F4.wireOp",EDGE,"E30")])]}),makeQuery(id+"F8.opExtrude","SWEPT_FACE",FACE,{"disambiguationData":[OSD([sQuery(id+"F7.wireOp",EDGE,"E67")])]})]});
            fillet(context, id + "F14", {"entities" : qUnion([Q0, Q1, Q2, Q3, Q4, Q5]), "radius" : 3 * mm, "tangentPropagation" : true, "allowEdgeOverflow" : false});
        }
        {
            var Q0;
            Q0=makeQuery(id+"F1.opExtrude","CAP_EDGE",EDGE,{"disambiguationData":[OSD([sQuery(id+"F0.wireOp",EDGE,"E1.bottom")])],"isStart":false});
            fillet(context, id + "F15", {"entities" : qUnion([Q0]), "radius" : 2 * mm, "tangentPropagation" : true, "allowEdgeOverflow" : false});
        }
        {
            var Q0;
            {var subQ0=sQuery(id+"F0.wireOp",EDGE,"E22.filletArc");var subQ1=sQuery(id+"F0.wireOp",EDGE,"E7");var subQ2=sQuery(id+"F0.wireOp",EDGE,"E6");var subQ3=sQuery(id+"F0.wireOp",EDGE,"E5");var subQ4=sQuery(id+"F0.wireOp",EDGE,"E4");var subQ5=sQuery(id+"F0.wireOp",EDGE,"E1.bottom");var subQ6=sQuery(id+"F0.wireOp",EDGE,"E21.filletArc");var subQ7=sQuery(id+"F0.wireOp",EDGE,"E1.top");var subQ8=sQuery(id+"F0.wireOp",EDGE,"E1.left");var subQ9=sQuery(id+"F0.wireOp",EDGE,"E1.right");var subQ10=sQuery(id+"F0.wireOp",EDGE,"E23.filletArc");var subQ11=sQuery(id+"F0.wireOp",EDGE,"E24.filletArc");Q0=makeQuery(id+"F2.boolean.opBoolean","SPLIT",FACE,{"disambiguationData":[TD([makeQuery(id+"F1.opExtrude","SWEPT_FACE",FACE,{"disambiguationData":[OSD([subQ5])]})])],"derivedFrom":makeQuery(id+"F1.opExtrude","CAP_FACE",FACE,{"disambiguationData":[OSD([subQ5,subQ7,subQ8,subQ9,subQ4,subQ3,subQ2,subQ1,subQ6,subQ0,subQ10,subQ11])],"isStart":true})});}
            var sketch = newSketch(context, id + "F16", { "sketchPlane" : qUnion([Q0])});
            skLineSegment(sketch, "E79.0", {"start": v(-80, 80) * mm, "end": v(80, 80) * mm});
            skArc(sketch, "E79.1", {"start": v(-80, 80) * mm, "mid": v(-87.07, 77.07) * mm, "end": v(-90, 70) * mm});
            skLineSegment(sketch, "E79.2", {"start": v(-90, -70) * mm, "end": v(-90, 70) * mm});
            skArc(sketch, "E79.3", {"start": v(-90, -70) * mm, "mid": v(-87.07, -77.07) * mm, "end": v(-80, -80) * mm});
            skLineSegment(sketch, "E79.4", {"start": v(-80, -80) * mm, "end": v(80, -80) * mm});
            skArc(sketch, "E79.5", {"start": v(80, -80) * mm, "mid": v(87.07, -77.07) * mm, "end": v(90, -70) * mm});
            skLineSegment(sketch, "E79.6", {"start": v(90, -70) * mm, "end": v(90, 70) * mm});
            skArc(sketch, "E79.7", {"start": v(90, 70) * mm, "mid": v(87.07, 77.07) * mm, "end": v(80, 80) * mm});
            skArc(sketch, "E79.8", {"start": v(52.38, 47.01) * mm, "mid": v(0, 53.33) * mm, "end": v(-52.38, 47.01) * mm});
            skArc(sketch, "E79.9", {"start": v(-52.38, 47.01) * mm, "mid": v(-57.87, 43.47) * mm, "end": v(-60, 37.3) * mm});
            skLineSegment(sketch, "E79.10", {"start": v(-60, 37.3) * mm, "end": v(-60, -37.3) * mm});
            skArc(sketch, "E79.11", {"start": v(-52.38, -47.01) * mm, "mid": v(0, -53.33) * mm, "end": v(52.38, -47.01) * mm});
            skArc(sketch, "E79.12", {"start": v(-60, -37.3) * mm, "mid": v(-57.87, -43.47) * mm, "end": v(-52.38, -47.01) * mm});
            skArc(sketch, "E79.13", {"start": v(52.38, -47.01) * mm, "mid": v(57.87, -43.47) * mm, "end": v(60, -37.3) * mm});
            skLineSegment(sketch, "E79.14", {"start": v(60, 37.3) * mm, "end": v(60, -37.3) * mm});
            skArc(sketch, "E79.15", {"start": v(60, 37.3) * mm, "mid": v(57.87, 43.47) * mm, "end": v(52.38, 47.01) * mm});
            skLineSegment(sketch, "E80", {"start": v(0, 80) * mm, "end": v(0, 110.2) * mm});
            skLineSegment(sketch, "E81", {"start": v(-33, 80) * mm, "end": v(-15, 98) * mm});
            skLineSegment(sketch, "E82", {"start": v(-15, 98) * mm, "end": v(-15, 110) * mm});
            skLineSegment(sketch, "E83", {"start": v(33, 80) * mm, "end": v(15, 98) * mm});
            skLineSegment(sketch, "E84", {"start": v(15, 98) * mm, "end": v(15, 110.2) * mm});
            skCircle(sketch, "E85", {"center": v(0, 110.2) * mm, "radius": 6 * mm});
            skArc(sketch, "E86", {"start": v(15, 110.2) * mm, "mid": v(-0.1, 125.19) * mm, "end": v(-15, 110) * mm});
            skLineSegment(sketch, "E87", {"start": v(-90, 0) * mm, "end": v(90, 0) * mm, "construction": true});
            skLineSegment(sketch, "E88.MirrorCS", {"start": v(-33, -80) * mm, "end": v(-15, -98) * mm});
            skLineSegment(sketch, "E89.MirrorCS", {"start": v(-15, -98) * mm, "end": v(-15, -110) * mm});
            skArc(sketch, "E90.MirrorCS", {"start": v(15, -110.2) * mm, "mid": v(-0.1, -125.19) * mm, "end": v(-15, -110) * mm});
            skLineSegment(sketch, "E91.MirrorCS", {"start": v(15, -98) * mm, "end": v(15, -110.2) * mm});
            skLineSegment(sketch, "E92.MirrorCS", {"start": v(33, -80) * mm, "end": v(15, -98) * mm});
            skLineSegment(sketch, "E93.MirrorCS", {"start": v(0, -80) * mm, "end": v(0, -110.2) * mm});
            skCircle(sketch, "E94.MirrorC", {"center": v(0, -110.2) * mm, "radius": 6 * mm});
            skSolve(sketch);
        }
        {
            var Q0;
            Q0 = qSketchRegion(id + "F16", true);
            var Q1;
            Q1=makeQuery(id+"F2.opExtrude","CAP_FACE",FACE,{"disambiguationData":[OSD([sQuery(id+"F0.wireOp",EDGE,"E12"),sQuery(id+"F0.wireOp",EDGE,"E13"),sQuery(id+"F0.wireOp",EDGE,"E14"),sQuery(id+"F0.wireOp",EDGE,"E15"),sQuery(id+"F0.wireOp",EDGE,"E17.filletArc"),sQuery(id+"F0.wireOp",EDGE,"E18.filletArc"),sQuery(id+"F0.wireOp",EDGE,"E19.filletArc"),sQuery(id+"F0.wireOp",EDGE,"E20.filletArc"),sQuery(id+"F0.wireOp",EDGE,"E25.0"),sQuery(id+"F0.wireOp",EDGE,"E25.1"),sQuery(id+"F0.wireOp",EDGE,"E25.2"),sQuery(id+"F0.wireOp",EDGE,"E25.3"),sQuery(id+"F0.wireOp",EDGE,"E25.4"),sQuery(id+"F0.wireOp",EDGE,"E25.5"),sQuery(id+"F0.wireOp",EDGE,"E25.6"),sQuery(id+"F0.wireOp",EDGE,"E25.7")])],"isStart":false});
            extrude(context, id + "F17", {"entities" : qUnion([Q0]), "endBound" : BoundingType.UP_TO_SURFACE, "endBoundEntityFace" : qUnion([Q1]), "depth" : 25 * mm});
        }
    });
